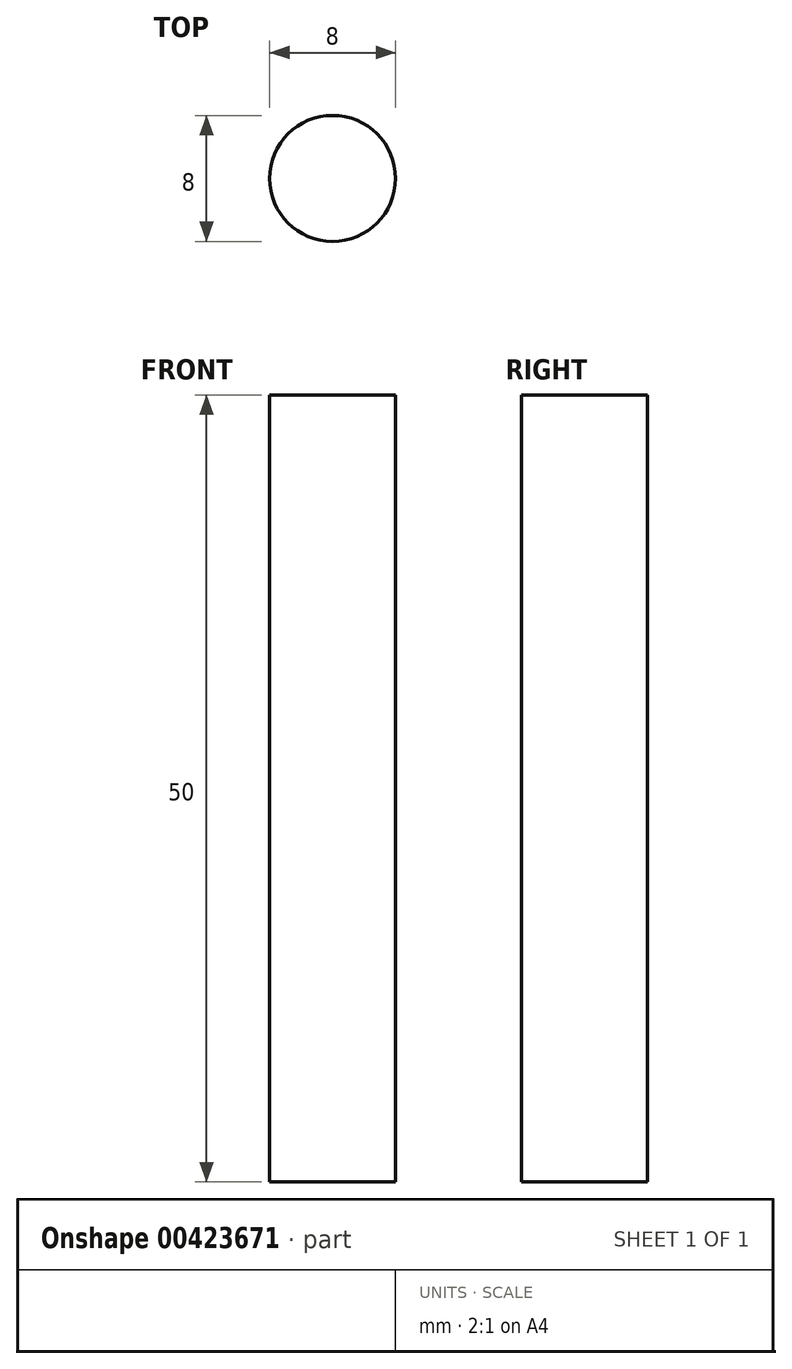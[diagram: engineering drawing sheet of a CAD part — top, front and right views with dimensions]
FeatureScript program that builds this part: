
annotation { "Feature Type Name" : "Feature", "Feature Type Description" : "" }
export const myFeature = defineFeature(function(context is Context, id is Id, definition is map)
    precondition{}
    {
        {
            var Q0;
            Q0=qCreatedBy(makeId("Top.planeOp"),FACE);
            var sketch = newSketch(context, id + "F0", { "sketchPlane" : qUnion([Q0])});
            skCircle(sketch, "E0", {"center": v(1.44, 0) * mm, "radius": 4 * mm});
            skSolve(sketch);
        }
        {
            var Q0;
            Q0=makeQuery(id+"F0.imprint","IMPRINT",FACE,{"disambiguationData":[TD([[makeQuery(id+"F0.imprint","IMPRINT",EDGE,{"derivedFrom":sQuery(id+"F0.wireOp",EDGE,"E0")}),1.0]])]});
            extrude(context, id + "F1", {"entities" : qUnion([Q0]), "depth" : 50 * mm});
        }
    });
